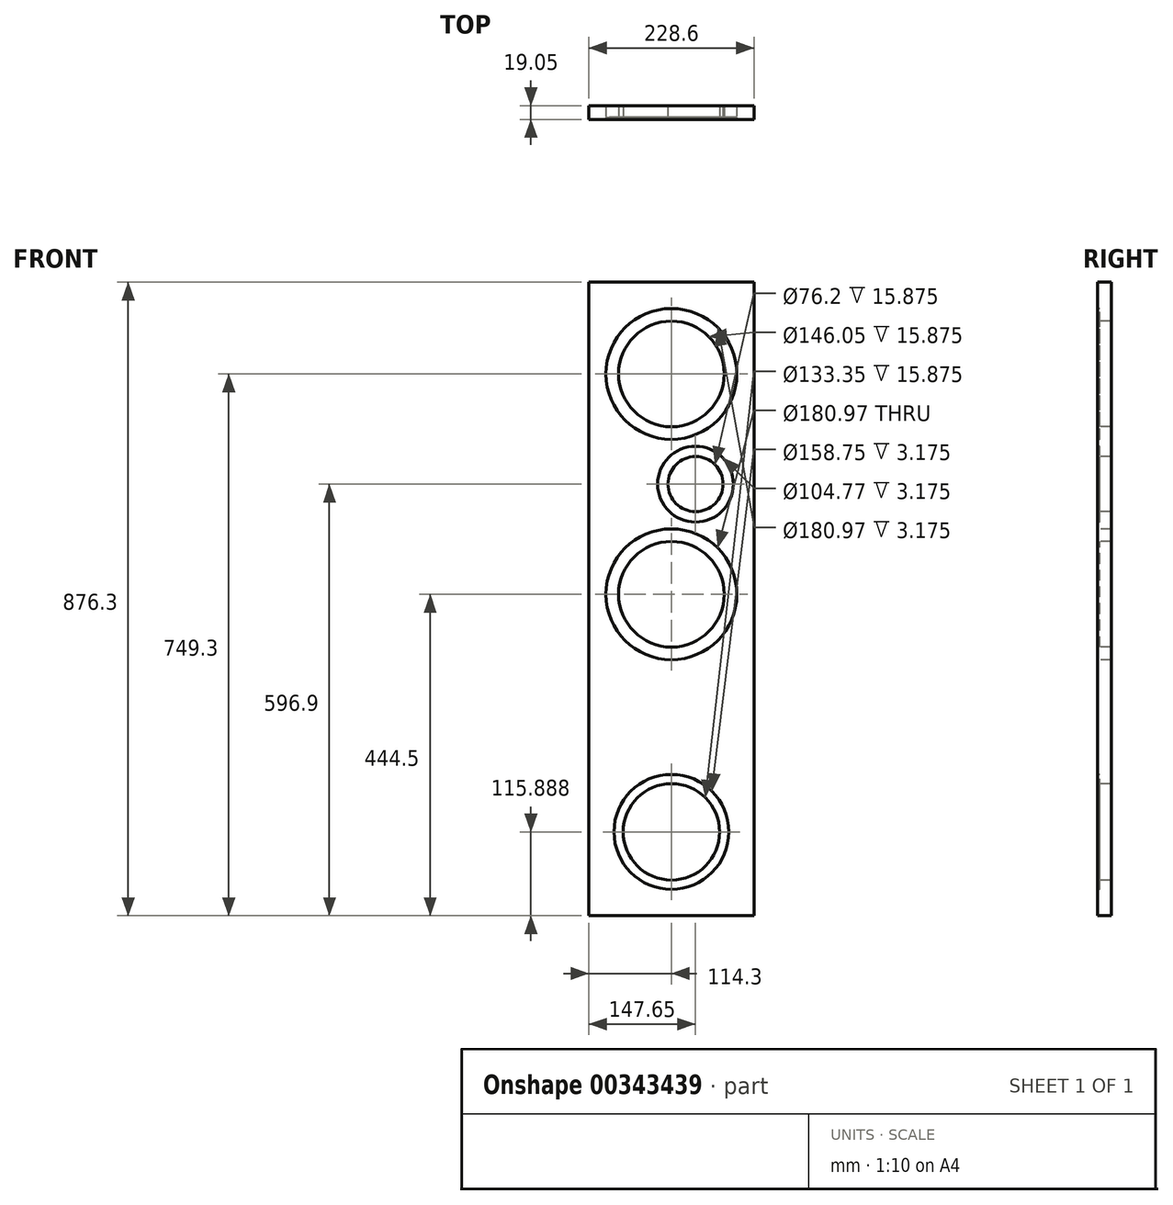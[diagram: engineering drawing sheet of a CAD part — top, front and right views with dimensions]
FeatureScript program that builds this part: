
annotation { "Feature Type Name" : "Feature", "Feature Type Description" : "" }
export const myFeature = defineFeature(function(context is Context, id is Id, definition is map)
    precondition{}
    {
        {
            var Q0;
            Q0=qCreatedBy(makeId("Front.planeOp"),FACE);
            var sketch = newSketch(context, id + "F0", { "sketchPlane" : qUnion([Q0])});
            skLineSegment(sketch, "E0.bottom", {"start": v(-114.3, 914.4) * mm, "end": v(114.3, 914.4) * mm});
            skLineSegment(sketch, "E0.top", {"start": v(-114.3, 38.1) * mm, "end": v(114.3, 38.1) * mm});
            skLineSegment(sketch, "E0.left", {"start": v(-114.3, 914.4) * mm, "end": v(-114.3, 38.1) * mm});
            skLineSegment(sketch, "E0.right", {"start": v(114.3, 914.4) * mm, "end": v(114.3, 38.1) * mm});
            skCircle(sketch, "E1", {"center": v(0, 787.4) * mm, "radius": 90.49 * mm});
            skCircle(sketch, "E2", {"center": v(33.35, 635) * mm, "radius": 38.1 * mm});
            skCircle(sketch, "E3", {"center": v(0, 787.4) * mm, "radius": 73.03 * mm});
            skCircle(sketch, "E4", {"center": v(33.35, 635) * mm, "radius": 52.39 * mm});
            skLineSegment(sketch, "E5", {"start": v(307.03, 635) * mm, "end": v(439.89, 635) * mm});
            skCircle(sketch, "E6.MirrorC", {"center": v(0, 482.6) * mm, "radius": 73.03 * mm});
            skCircle(sketch, "E7.MirrorC", {"center": v(0, 482.6) * mm, "radius": 90.49 * mm});
            skLineSegment(sketch, "E8", {"start": v(299.18, 355.6) * mm, "end": v(426.8, 355.6) * mm});
            skCircle(sketch, "E9", {"center": v(0, 153.99) * mm, "radius": 79.38 * mm});
            skLineSegment(sketch, "E10", {"start": v(333.82, 877.89) * mm, "end": v(430.62, 877.89) * mm});
            skLineSegment(sketch, "E11", {"start": v(409.67, 74.61) * mm, "end": v(278.97, 74.61) * mm});
            skLineSegment(sketch, "E12", {"start": v(430.62, 877.89) * mm, "end": v(430.62, 914.4) * mm});
            skLineSegment(sketch, "E13", {"start": v(409.67, 74.61) * mm, "end": v(409.67, 38.1) * mm});
            skCircle(sketch, "E14", {"center": v(0, 153.99) * mm, "radius": 66.68 * mm});
            skLineSegment(sketch, "E15", {"start": v(323.31, 692.15) * mm, "end": v(428.61, 692.15) * mm});
            skLineSegment(sketch, "E16", {"start": v(428.61, 687.39) * mm, "end": v(321.83, 687.39) * mm});
            skLineSegment(sketch, "E17", {"start": v(321.83, 696.91) * mm, "end": v(434.54, 696.91) * mm});
            skLineSegment(sketch, "E18", {"start": v(307.98, 392.11) * mm, "end": v(424.03, 392.11) * mm});
            skSolve(sketch);
        }
        {
            var Q0;
            Q0=makeQuery(id+"F0.imprint","IMPRINT",FACE,{"disambiguationData":[TD([[makeQuery(id+"F0.imprint","IMPRINT",EDGE,{"derivedFrom":sQuery(id+"F0.wireOp",EDGE,"E0.bottom")}),-1.0]])]});
            var Q1;
            Q1=makeQuery(id+"F0.imprint","IMPRINT",FACE,{"disambiguationData":[TD([[makeQuery(id+"F0.imprint","IMPRINT",EDGE,{"derivedFrom":sQuery(id+"F0.wireOp",EDGE,"E1")}),1.0]])]});
            var Q2;
            Q2=makeQuery(id+"F0.imprint","IMPRINT",FACE,{"disambiguationData":[TD([[makeQuery(id+"F0.imprint","IMPRINT",EDGE,{"derivedFrom":sQuery(id+"F0.wireOp",EDGE,"E2")}),-1.0]])]});
            var Q3;
            Q3=makeQuery(id+"F0.imprint","IMPRINT",FACE,{"disambiguationData":[TD([[makeQuery(id+"F0.imprint","IMPRINT",EDGE,{"derivedFrom":sQuery(id+"F0.wireOp",EDGE,"E6.MirrorC")}),1.0]])]});
            var Q4;
            Q4=makeQuery(id+"F0.imprint","IMPRINT",FACE,{"disambiguationData":[TD([[makeQuery(id+"F0.imprint","IMPRINT",EDGE,{"derivedFrom":sQuery(id+"F0.wireOp",EDGE,"E9")}),1.0]])]});
            extrude(context, id + "F1", {"entities" : qUnion([Q0, Q1, Q2, Q3, Q4]), "oppositeDirection" : true, "depth" : 19.05 * mm});
        }
        {
            var Q0;
            Q0=makeQuery(id+"F0.imprint","IMPRINT",FACE,{"disambiguationData":[TD([[makeQuery(id+"F0.imprint","IMPRINT",EDGE,{"derivedFrom":sQuery(id+"F0.wireOp",EDGE,"E1")}),1.0]])]});
            var Q1;
            Q1=makeQuery(id+"F0.imprint","IMPRINT",FACE,{"disambiguationData":[TD([[makeQuery(id+"F0.imprint","IMPRINT",EDGE,{"derivedFrom":sQuery(id+"F0.wireOp",EDGE,"E2")}),-1.0]])]});
            var Q2;
            Q2=makeQuery(id+"F0.imprint","IMPRINT",FACE,{"disambiguationData":[TD([[makeQuery(id+"F0.imprint","IMPRINT",EDGE,{"derivedFrom":sQuery(id+"F0.wireOp",EDGE,"E6.MirrorC")}),1.0]])]});
            var Q3;
            Q3=makeQuery(id+"F0.imprint","IMPRINT",FACE,{"disambiguationData":[TD([[makeQuery(id+"F0.imprint","IMPRINT",EDGE,{"derivedFrom":sQuery(id+"F0.wireOp",EDGE,"E9")}),1.0]])]});
            extrude(context, id + "F2", {"entities" : qUnion([Q0, Q1, Q2, Q3]), "operationType" : NewBodyOperationType.REMOVE, "oppositeDirection" : true, "depth" : 3.17 * mm});
        }
        {
            var Q0;
            Q0=qCreatedBy(makeId("Top.planeOp"),FACE);
            var sketch = newSketch(context, id + "F3", { "sketchPlane" : qUnion([Q0])});
            skLineSegment(sketch, "E19.bottom", {"start": v(-114.3, 0) * mm, "end": v(114.3, 0) * mm});
            skLineSegment(sketch, "E19.top", {"start": v(-114.3, 514.35) * mm, "end": v(114.3, 514.35) * mm});
            skLineSegment(sketch, "E19.left", {"start": v(-114.3, 0) * mm, "end": v(-114.3, 514.35) * mm});
            skLineSegment(sketch, "E19.right", {"start": v(114.3, 0) * mm, "end": v(114.3, 514.35) * mm});
            skSolve(sketch);
        }
    });
